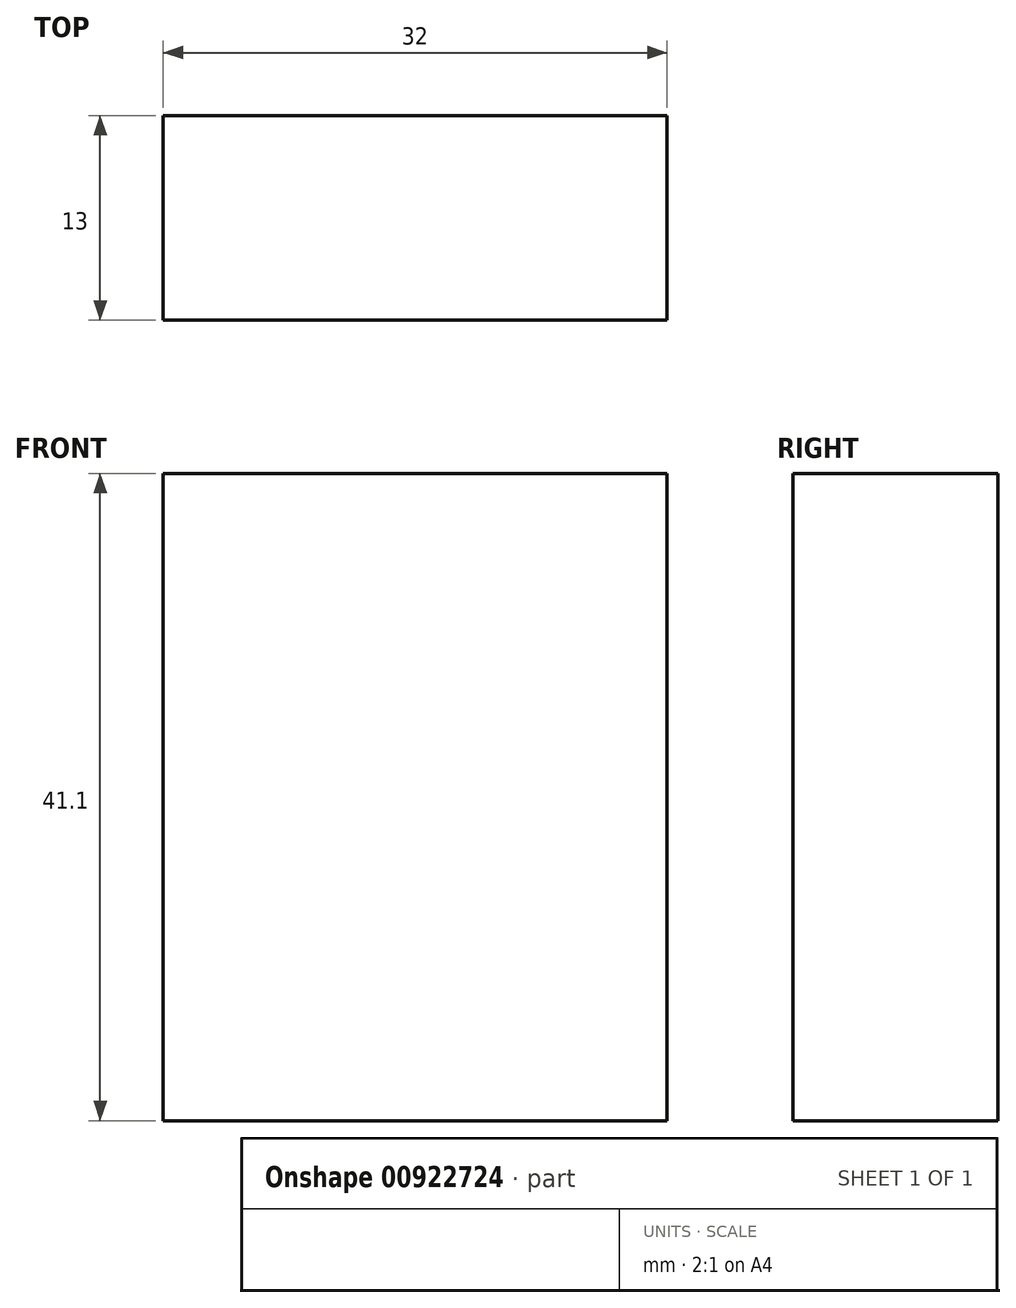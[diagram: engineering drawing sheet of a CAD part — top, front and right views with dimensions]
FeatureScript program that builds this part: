
annotation { "Feature Type Name" : "Feature", "Feature Type Description" : "" }
export const myFeature = defineFeature(function(context is Context, id is Id, definition is map)
    precondition{}
    {
        {
            var Q0;
            Q0=qCreatedBy(makeId("Front.planeOp"),FACE);
            var sketch = newSketch(context, id + "F0", { "sketchPlane" : qUnion([Q0])});
            skLineSegment(sketch, "E0.bottom", {"start": v(16, -20.55) * mm, "end": v(-16, -20.55) * mm});
            skLineSegment(sketch, "E0.top", {"start": v(16, 20.55) * mm, "end": v(-16, 20.55) * mm});
            skLineSegment(sketch, "E0.left", {"start": v(16, -20.55) * mm, "end": v(16, 20.55) * mm});
            skLineSegment(sketch, "E0.right", {"start": v(-16, -20.55) * mm, "end": v(-16, 20.55) * mm});
            skPoint(sketch, "E0.middle", {"position": v(0, 0) * mm});
            skSolve(sketch);
        }
        {
            var Q0;
            Q0 = qSketchRegion(id + "F0", true);
            extrude(context, id + "F1", {"entities" : qUnion([Q0]), "endBound" : BoundingType.SYMMETRIC, "depth" : 13 * mm, "offsetDistance" : 25 * mm});
        }
    });
